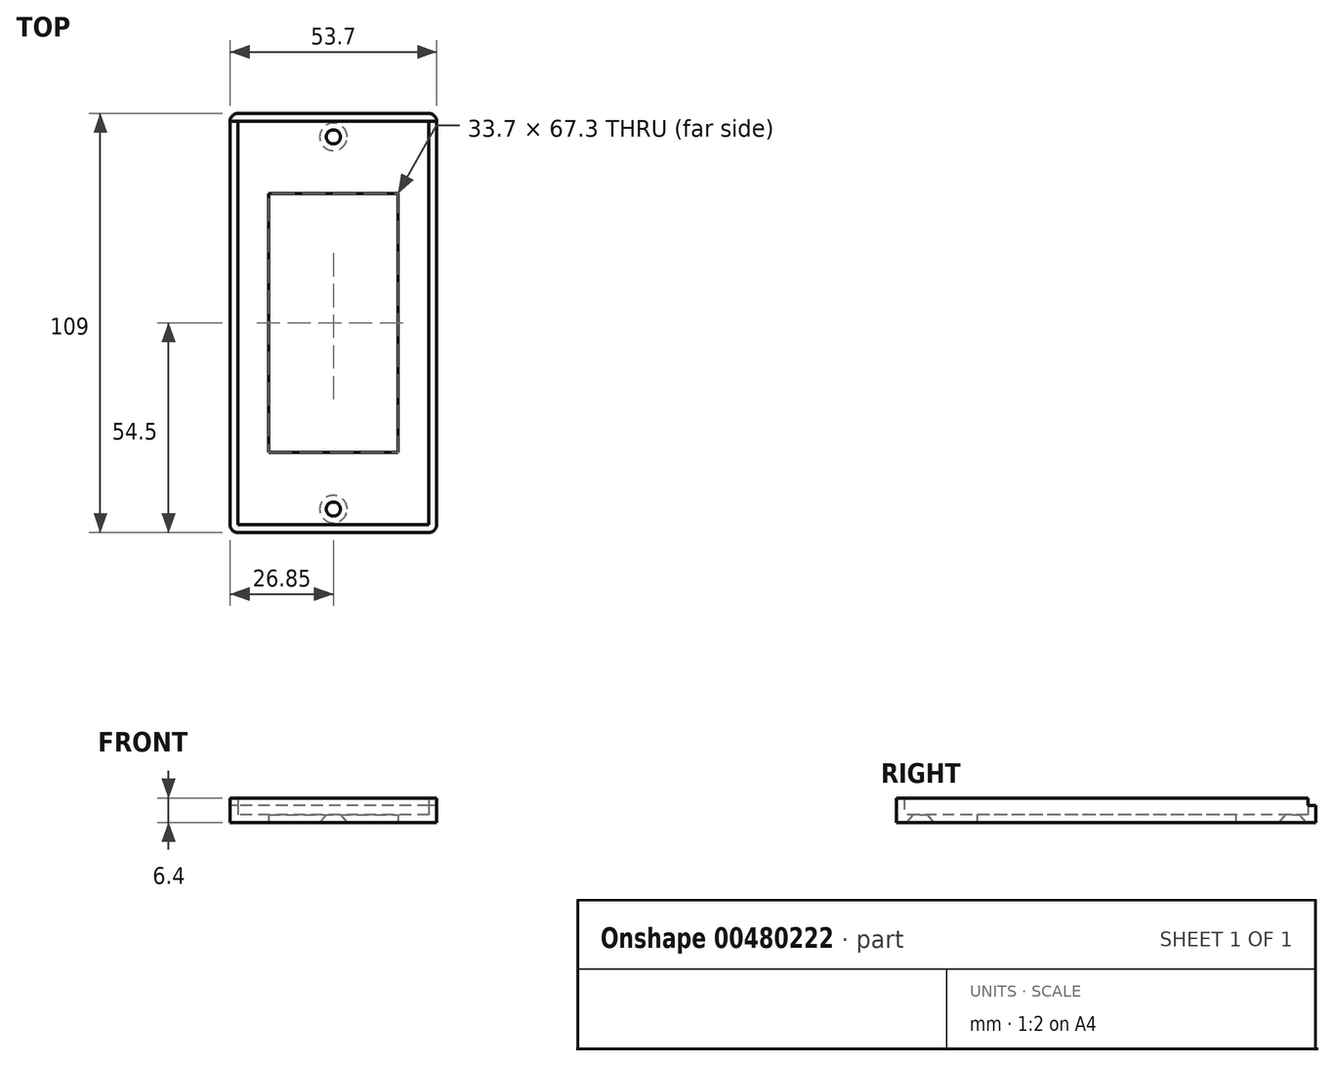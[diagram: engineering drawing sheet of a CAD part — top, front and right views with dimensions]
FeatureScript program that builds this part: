
annotation { "Feature Type Name" : "Feature", "Feature Type Description" : "" }
export const myFeature = defineFeature(function(context is Context, id is Id, definition is map)
    precondition{}
    {
        {
            var Q0;
            Q0=qCreatedBy(makeId("Top.planeOp"),FACE);
            var sketch = newSketch(context, id + "F0", { "sketchPlane" : qUnion([Q0])});
            skLineSegment(sketch, "E0.bottom", {"start": v(24.85, 52.5) * mm, "end": v(-24.85, 52.5) * mm});
            skLineSegment(sketch, "E0.top", {"start": v(24.85, -52.5) * mm, "end": v(-24.85, -52.5) * mm});
            skLineSegment(sketch, "E0.left", {"start": v(24.85, 52.5) * mm, "end": v(24.85, -52.5) * mm});
            skLineSegment(sketch, "E0.right", {"start": v(-24.85, 52.5) * mm, "end": v(-24.85, -52.5) * mm});
            skPoint(sketch, "E0.middle", {"position": v(0, 0) * mm});
            skPoint(sketch, "E1", {"position": v(0, 48.4) * mm});
            skPoint(sketch, "E2", {"position": v(0, -48.4) * mm});
            skLineSegment(sketch, "E3", {"start": v(0, 48.4) * mm, "end": v(0, -48.4) * mm, "construction": true});
            skLineSegment(sketch, "E4.bottom", {"start": v(-16.85, 33.65) * mm, "end": v(16.85, 33.65) * mm});
            skLineSegment(sketch, "E4.top", {"start": v(-16.85, -33.65) * mm, "end": v(16.85, -33.65) * mm});
            skLineSegment(sketch, "E4.left", {"start": v(-16.85, 33.65) * mm, "end": v(-16.85, -33.65) * mm});
            skLineSegment(sketch, "E4.right", {"start": v(16.85, 33.65) * mm, "end": v(16.85, -33.65) * mm});
            skLineSegment(sketch, "E5.0", {"start": v(26.85, 54.5) * mm, "end": v(-26.85, 54.5) * mm});
            skLineSegment(sketch, "E5.1", {"start": v(26.85, 54.5) * mm, "end": v(26.85, -54.5) * mm});
            skLineSegment(sketch, "E5.2", {"start": v(26.85, -54.5) * mm, "end": v(-26.85, -54.5) * mm});
            skLineSegment(sketch, "E5.3", {"start": v(-26.85, 54.5) * mm, "end": v(-26.85, -54.5) * mm});
            skLineSegment(sketch, "E6", {"start": v(-24.85, 52.5) * mm, "end": v(-26.85, 52.5) * mm});
            skLineSegment(sketch, "E7", {"start": v(24.85, 52.5) * mm, "end": v(26.85, 52.5) * mm});
            skSolve(sketch);
        }
        {
            var Q0;
            Q0=makeQuery(id+"F0.imprint","IMPRINT",FACE,{"disambiguationData":[TD([[makeQuery(id+"F0.imprint","IMPRINT",EDGE,{"derivedFrom":sQuery(id+"F0.wireOp",EDGE,"E0.bottom")}),1.0]])]});
            extrude(context, id + "F1", {"entities" : qUnion([Q0]), "depth" : 2 * mm});
        }
        {
            var Q0;
            Q0=makeQuery(id+"F0.imprint","IMPRINT",FACE,{"disambiguationData":[TD([[makeQuery(id+"F0.imprint","IMPRINT",EDGE,{"derivedFrom":sQuery(id+"F0.wireOp",EDGE,"E0.top")}),1.0]])]});
            extrude(context, id + "F2", {"entities" : qUnion([Q0]), "operationType" : NewBodyOperationType.ADD, "depth" : (6.4) * mm});
        }
        {
            var Q0;
            Q0=makeQuery(id+"F0.imprint","IMPRINT",FACE,{"disambiguationData":[TD([[makeQuery(id+"F0.imprint","IMPRINT",EDGE,{"derivedFrom":sQuery(id+"F0.wireOp",EDGE,"E0.bottom")}),-1.0]])]});
            extrude(context, id + "F3", {"entities" : qUnion([Q0]), "operationType" : NewBodyOperationType.ADD, "depth" : (6.4 - 2) * mm});
        }
        {
            var Q0;
            Q0=sQuery(id+"F0.wireOp",VERTEX,"E1");
            var Q1;
            Q1=sQuery(id+"F0.wireOp",VERTEX,"E2");
            var Q2;
            Q2=makeQuery(id+"F1.opExtrude","SWEPT_BODY",BODY,{"disambiguationData":[OSD([sQuery(id+"F0.wireOp",EDGE,"E0.bottom"),sQuery(id+"F0.wireOp",EDGE,"E0.top"),sQuery(id+"F0.wireOp",EDGE,"E0.left"),sQuery(id+"F0.wireOp",EDGE,"E0.right"),sQuery(id+"F0.wireOp",EDGE,"E4.bottom"),sQuery(id+"F0.wireOp",EDGE,"E4.top"),sQuery(id+"F0.wireOp",EDGE,"E4.left"),sQuery(id+"F0.wireOp",EDGE,"E4.right")])]});
            hole(context, id + "F4", {"style" : HoleStyle.C_SINK, "endStyle" : HoleEndStyle.THROUGH, "oppositeDirection" : true, "standardTappedOrClearance" : lookupTablePath({ "standard" : "ANSI", "fit" : "Normal (ASME)", "size" : "#5", "type" : "Clearance" }), "standardBlindInLast" : lookupTablePath({ "fit" : "Free", "standard" : "ANSI", "size" : "#5", "type" : "Clearance" }), "holeDiameter" : 3.45 * mm, "cSinkDiameter" : 7.14 * mm, "cSinkAngle" : 82 * degree, "isTappedThrough" : true, "tappedDepth" : 12 * mm, "tapClearance" : 3, "locations" : qUnion([Q0, Q1]), "scope" : qUnion([Q2])});
        }
        {
            var Q0;
            Q0=makeQuery(id+"F3.opExtrude","SWEPT_EDGE",EDGE,{"disambiguationData":[OSD([sQuery(id+"F0.wireOp",EDGE,"E5.0"),sQuery(id+"F0.wireOp",EDGE,"E5.1")])]});
            var Q1;
            Q1=makeQuery(id+"F2.opExtrude","SWEPT_EDGE",EDGE,{"disambiguationData":[OSD([sQuery(id+"F0.wireOp",EDGE,"E5.1"),sQuery(id+"F0.wireOp",EDGE,"E5.2")])]});
            var Q2;
            Q2=makeQuery(id+"F2.opExtrude","SWEPT_EDGE",EDGE,{"disambiguationData":[OSD([sQuery(id+"F0.wireOp",EDGE,"E5.2"),sQuery(id+"F0.wireOp",EDGE,"E5.3")])]});
            var Q3;
            Q3=makeQuery(id+"F3.opExtrude","SWEPT_EDGE",EDGE,{"disambiguationData":[OSD([sQuery(id+"F0.wireOp",EDGE,"E5.0"),sQuery(id+"F0.wireOp",EDGE,"E5.3")])]});
            fillet(context, id + "F5", {"entities" : qUnion([Q0, Q1, Q2, Q3]), "radius" : 2 * mm, "tangentPropagation" : true, "allowEdgeOverflow" : false});
        }
    });
